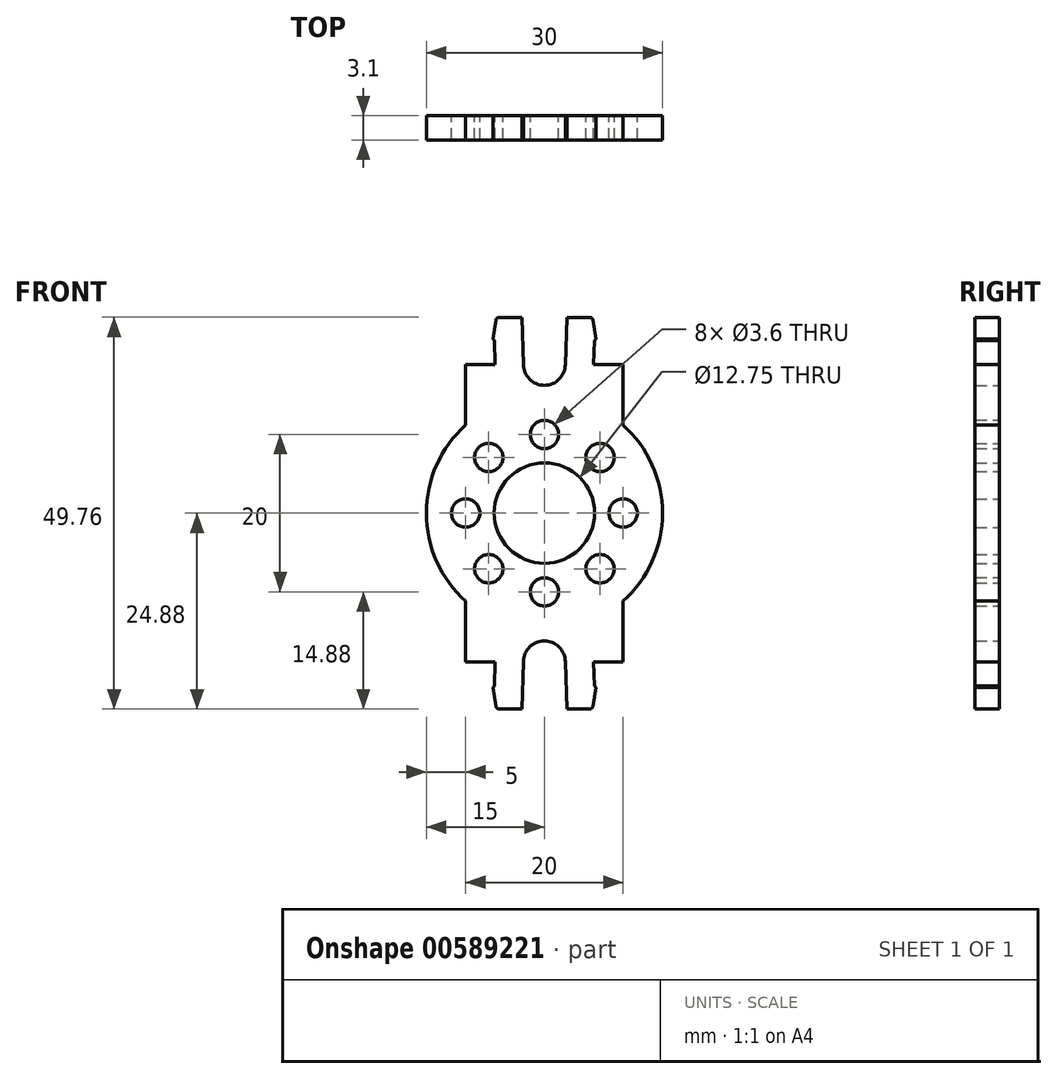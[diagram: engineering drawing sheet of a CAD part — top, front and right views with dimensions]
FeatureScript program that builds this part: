
annotation { "Feature Type Name" : "Feature", "Feature Type Description" : "" }
export const myFeature = defineFeature(function(context is Context, id is Id, definition is map)
    precondition{}
    {
        {
            var Q0;
            Q0=qCreatedBy(makeId("Front.planeOp"),FACE);
            var sketch = newSketch(context, id + "F0", { "sketchPlane" : qUnion([Q0])});
            skArc(sketch, "E0", {"start": v(-10, 11.18) * mm, "mid": v(-15, 0) * mm, "end": v(-10, -11.18) * mm});
            skLineSegment(sketch, "E1.bottom", {"start": v(-10, 18.88) * mm, "end": v(-6.25, 18.88) * mm});
            skLineSegment(sketch, "E1.left", {"start": v(-10, 18.88) * mm, "end": v(-10, 11.18) * mm});
            skLineSegment(sketch, "E1.right", {"start": v(10, 18.88) * mm, "end": v(10, 11.18) * mm});
            skPoint(sketch, "E1.middle", {"position": v(0, 15.03) * mm});
            skCircle(sketch, "E2", {"center": v(0, 0) * mm, "radius": 6.38 * mm});
            skCircle(sketch, "E3", {"center": v(-10, 0) * mm, "radius": 1.8 * mm});
            skCircle(sketch, "E4.1.0", {"center": v(-7.07, -7.07) * mm, "radius": 1.8 * mm});
            skCircle(sketch, "E4.2.0", {"center": v(0, -10) * mm, "radius": 1.8 * mm});
            skCircle(sketch, "E4.3.0", {"center": v(7.07, -7.07) * mm, "radius": 1.8 * mm});
            skCircle(sketch, "E4.4.0", {"center": v(10, 0) * mm, "radius": 1.8 * mm});
            skCircle(sketch, "E4.5.0", {"center": v(7.07, 7.07) * mm, "radius": 1.8 * mm});
            skCircle(sketch, "E4.6.0", {"center": v(0, 10) * mm, "radius": 1.8 * mm});
            skCircle(sketch, "E4.7.0", {"center": v(-7.07, 7.07) * mm, "radius": 1.8 * mm});
            skLineSegment(sketch, "E5.MirrorCS", {"start": v(-10, -18.88) * mm, "end": v(-6.25, -18.88) * mm});
            skLineSegment(sketch, "E6.MirrorCS", {"start": v(10, -18.88) * mm, "end": v(10, -11.18) * mm});
            skArc(sketch, "E7.trimOffspring", {"start": v(10, -11.18) * mm, "mid": v(15, 0) * mm, "end": v(10, 11.18) * mm});
            skArc(sketch, "E8", {"start": v(2.65, -18.88) * mm, "mid": v(0, -16.23) * mm, "end": v(-2.65, -18.88) * mm});
            skLineSegment(sketch, "E9", {"start": v(-2.65, -18.88) * mm, "end": v(-2.88, -24.88) * mm});
            skLineSegment(sketch, "E10", {"start": v(-2.88, -24.88) * mm, "end": v(-5.76, -24.88) * mm});
            skLineSegment(sketch, "E11", {"start": v(-6.15, -24.54) * mm, "end": v(-6.52, -22.13) * mm});
            skLineSegment(sketch, "E12", {"start": v(-6.52, -22.13) * mm, "end": v(-6.37, -21.93) * mm});
            skLineSegment(sketch, "E13", {"start": v(-6.37, -21.93) * mm, "end": v(-6.25, -18.88) * mm});
            skPoint(sketch, "E14.visualSharp", {"position": v(-6.1, -24.88) * mm});
            skArc(sketch, "E14.filletArc", {"start": v(-6.15, -24.54) * mm, "mid": v(-6.02, -24.78) * mm, "end": v(-5.76, -24.88) * mm});
            skLineSegment(sketch, "E15.trimOffspring", {"start": v(6.25, -18.88) * mm, "end": v(10, -18.88) * mm});
            skArc(sketch, "E16.MirrorCS", {"start": v(6.15, -24.54) * mm, "mid": v(6.02, -24.78) * mm, "end": v(5.76, -24.88) * mm});
            skLineSegment(sketch, "E17.MirrorCS", {"start": v(2.65, -18.88) * mm, "end": v(2.88, -24.88) * mm});
            skLineSegment(sketch, "E18.MirrorCS", {"start": v(6.15, -24.54) * mm, "end": v(6.52, -22.13) * mm});
            skLineSegment(sketch, "E19.MirrorCS", {"start": v(6.37, -21.93) * mm, "end": v(6.25, -18.88) * mm});
            skLineSegment(sketch, "E20.MirrorCS", {"start": v(6.53, -22.13) * mm, "end": v(6.37, -21.93) * mm});
            skPoint(sketch, "E21.MirrorP", {"position": v(6.1, -24.88) * mm});
            skLineSegment(sketch, "E22.MirrorCS", {"start": v(2.88, -24.88) * mm, "end": v(5.76, -24.88) * mm});
            skArc(sketch, "E23.MirrorCS", {"start": v(6.15, 24.54) * mm, "mid": v(6.02, 24.78) * mm, "end": v(5.76, 24.88) * mm});
            skArc(sketch, "E24.MirrorCS", {"start": v(-6.15, 24.54) * mm, "mid": v(-6.02, 24.78) * mm, "end": v(-5.76, 24.88) * mm});
            skLineSegment(sketch, "E25.MirrorCS", {"start": v(6.52, 22.12) * mm, "end": v(6.37, 21.93) * mm});
            skLineSegment(sketch, "E26.MirrorCS", {"start": v(-2.65, 18.87) * mm, "end": v(-2.88, 24.88) * mm});
            skLineSegment(sketch, "E27.MirrorCS", {"start": v(-6.37, 21.93) * mm, "end": v(-6.25, 18.88) * mm});
            skLineSegment(sketch, "E28.MirrorCS", {"start": v(2.88, 24.88) * mm, "end": v(5.76, 24.88) * mm});
            skLineSegment(sketch, "E29.MirrorCS", {"start": v(-6.52, 22.13) * mm, "end": v(-6.37, 21.93) * mm});
            skLineSegment(sketch, "E30.MirrorCS", {"start": v(2.65, 18.88) * mm, "end": v(2.88, 24.88) * mm});
            skPoint(sketch, "E31.MirrorP", {"position": v(6.1, 24.88) * mm});
            skLineSegment(sketch, "E32.MirrorCS", {"start": v(6.37, 21.93) * mm, "end": v(6.25, 18.88) * mm});
            skLineSegment(sketch, "E33.MirrorCS", {"start": v(6.15, 24.54) * mm, "end": v(6.52, 22.13) * mm});
            skLineSegment(sketch, "E34.MirrorCS", {"start": v(-6.15, 24.54) * mm, "end": v(-6.52, 22.13) * mm});
            skLineSegment(sketch, "E35.MirrorCS", {"start": v(-2.88, 24.88) * mm, "end": v(-5.76, 24.88) * mm});
            skPoint(sketch, "E36.MirrorP", {"position": v(-6.1, 24.88) * mm});
            skLineSegment(sketch, "E37.trimOffspring", {"start": v(6.25, 18.88) * mm, "end": v(10, 18.88) * mm});
            skArc(sketch, "E38.MirrorCS", {"start": v(2.65, 18.88) * mm, "mid": v(0, 16.23) * mm, "end": v(-2.65, 18.88) * mm});
            skLineSegment(sketch, "E39", {"start": v(-10, -11.18) * mm, "end": v(-10, -18.88) * mm});
            skSolve(sketch);
        }
        {
            var Q0;
            Q0=makeQuery(id+"F0.imprint","IMPRINT",FACE,{"disambiguationData":[TD([[makeQuery(id+"F0.imprint","IMPRINT",EDGE,{"derivedFrom":sQuery(id+"F0.wireOp",EDGE,"E0")}),1.0]])]});
            extrude(context, id + "F1", {"entities" : qUnion([Q0]), "depth" : 3.1 * mm, "offsetDistance" : 25 * mm});
        }
    });
